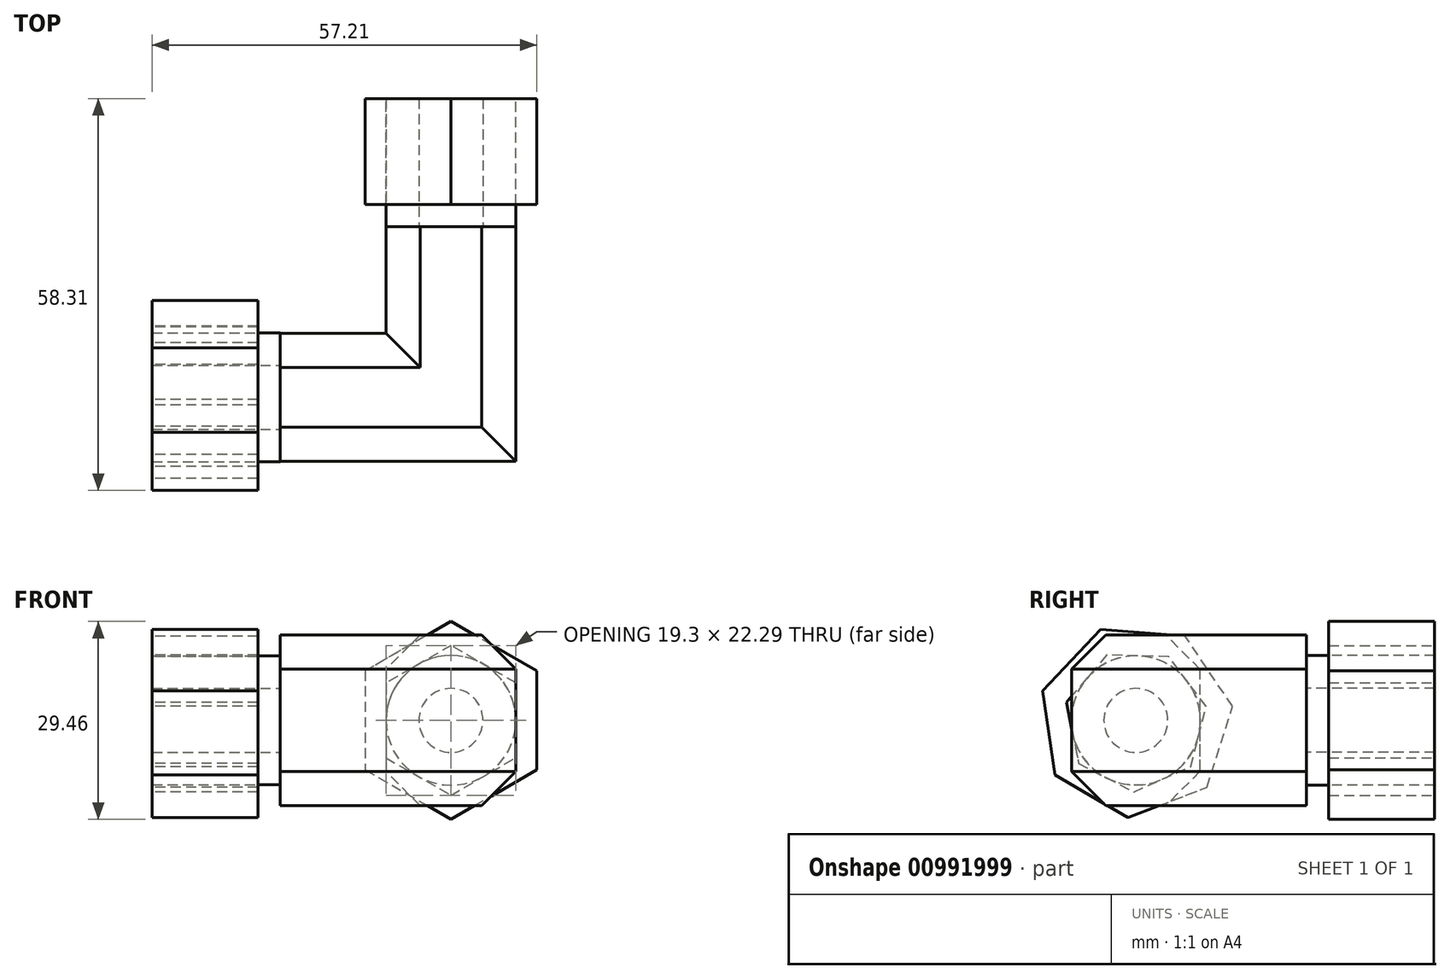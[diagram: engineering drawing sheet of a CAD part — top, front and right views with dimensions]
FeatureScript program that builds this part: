
annotation { "Feature Type Name" : "Feature", "Feature Type Description" : "" }
export const myFeature = defineFeature(function(context is Context, id is Id, definition is map)
    precondition{}
    {
        {
            var Q0;
            Q0=qCreatedBy(makeId("Top.planeOp"),FACE);
            var sketch = newSketch(context, id + "F0", { "sketchPlane" : qUnion([Q0])});
            skLineSegment(sketch, "E0", {"start": v(0, 0) * mm, "end": v(0, 25.4) * mm, "construction": true});
            skLineSegment(sketch, "E1", {"start": v(0, 0) * mm, "end": v(-25.4, 0) * mm, "construction": true});
            skLineSegment(sketch, "E2", {"start": v(-25.4, 9.52) * mm, "end": v(-9.65, 9.53) * mm});
            skLineSegment(sketch, "E3", {"start": v(-9.65, 9.53) * mm, "end": v(-9.65, 25.4) * mm});
            skLineSegment(sketch, "E4", {"start": v(-9.65, 25.4) * mm, "end": v(0, 25.4) * mm});
            skLineSegment(sketch, "E5", {"start": v(-25.4, 9.52) * mm, "end": v(-25.4, 0) * mm});
            skLineSegment(sketch, "E6.MirrorCS", {"start": v(9.65, 9.53) * mm, "end": v(9.65, 25.4) * mm});
            skLineSegment(sketch, "E7.MirrorCS", {"start": v(9.65, 25.4) * mm, "end": v(0, 25.4) * mm});
            skLineSegment(sketch, "E8.MirrorCS", {"start": v(-25.4, -9.53) * mm, "end": v(-25.4, 0) * mm});
            skLineSegment(sketch, "E9", {"start": v(-25.4, -9.53) * mm, "end": v(9.65, -9.53) * mm});
            skLineSegment(sketch, "E10", {"start": v(9.65, -9.53) * mm, "end": v(9.65, 9.53) * mm});
            skSolve(sketch);
        }
        {
            var Q0;
            Q0=makeQuery(id+"F0.imprint","IMPRINT",FACE,{"disambiguationData":[TD([[makeQuery(id+"F0.imprint","IMPRINT",EDGE,{"derivedFrom":sQuery(id+"F0.wireOp",EDGE,"E2")}),-1.0]])]});
            extrude(context, id + "F1", {"entities" : qUnion([Q0]), "endBound" : BoundingType.SYMMETRIC, "depth" : 25.4 * mm, "offsetDistance" : 25.4 * mm});
        }
        {
            var Q0;
            Q0=makeQuery(id+"F1.opExtrude","SWEPT_FACE",FACE,{"disambiguationData":[OSD([sQuery(id+"F0.wireOp",EDGE,"E5"),sQuery(id+"F0.wireOp",EDGE,"E8.MirrorCS")])]});
            var sketch = newSketch(context, id + "F2", { "sketchPlane" : qUnion([Q0])});
            skCircle(sketch, "E11", {"center": v(0, 0) * mm, "radius": 9.6 * mm});
            skCircle(sketch, "E12", {"center": v(0, 0) * mm, "radius": 4.76 * mm});
            skSolve(sketch);
        }
        {
            var Q0;
            Q0 = qSketchRegion(id + "F2", true);
            extrude(context, id + "F3", {"entities" : qUnion([Q0]), "operationType" : NewBodyOperationType.ADD, "depth" : 19.05 * mm, "offsetDistance" : 25.4 * mm});
        }
        {
            var Q0;
            Q0=makeQuery(id+"F3.opExtrude","CAP_FACE",FACE,{"disambiguationData":[OSD([sQuery(id+"F2.wireOp",EDGE,"E11"),sQuery(id+"F2.wireOp",EDGE,"E12")])],"isStart":false});
            var sketch = newSketch(context, id + "F4", { "sketchPlane" : qUnion([Q0])});
            skCircle(sketch, "E13.cCircle", {"center": v(0, 0) * mm, "radius": 9.6 * mm, "construction": true});
            skLineSegment(sketch, "E13.0", {"start": v(10.32, 2.66) * mm, "end": v(8.52, -6.41) * mm});
            skLineSegment(sketch, "E13.1", {"start": v(8.52, -6.41) * mm, "end": v(0.3, -10.66) * mm});
            skLineSegment(sketch, "E13.2", {"start": v(0.3, -10.66) * mm, "end": v(-8.15, -6.88) * mm});
            skLineSegment(sketch, "E13.3", {"start": v(-8.15, -6.88) * mm, "end": v(-10.46, 2.08) * mm});
            skLineSegment(sketch, "E13.4", {"start": v(-10.46, 2.08) * mm, "end": v(-4.9, 9.47) * mm});
            skLineSegment(sketch, "E13.5", {"start": v(-4.9, 9.47) * mm, "end": v(4.35, 9.73) * mm});
            skLineSegment(sketch, "E13.6", {"start": v(4.35, 9.73) * mm, "end": v(10.32, 2.66) * mm});
            skPoint(sketch, "E13.0.midPoint", {"position": v(9.42, -1.87) * mm});
            skCircle(sketch, "E14.cCircle", {"center": v(0, 0) * mm, "radius": 13.1 * mm, "construction": true});
            skLineSegment(sketch, "E14.0", {"start": v(13.86, 4.37) * mm, "end": v(12.05, -8.11) * mm});
            skLineSegment(sketch, "E14.1", {"start": v(12.05, -8.11) * mm, "end": v(1.17, -14.48) * mm});
            skLineSegment(sketch, "E14.2", {"start": v(1.17, -14.48) * mm, "end": v(-10.6, -9.95) * mm});
            skLineSegment(sketch, "E14.3", {"start": v(-10.6, -9.95) * mm, "end": v(-14.38, 2.08) * mm});
            skLineSegment(sketch, "E14.4", {"start": v(-14.38, 2.08) * mm, "end": v(-7.34, 12.54) * mm});
            skLineSegment(sketch, "E14.5", {"start": v(-7.34, 12.54) * mm, "end": v(5.23, 13.56) * mm});
            skLineSegment(sketch, "E14.6", {"start": v(5.23, 13.56) * mm, "end": v(13.86, 4.37) * mm});
            skPoint(sketch, "E14.0.midPoint", {"position": v(12.96, -1.87) * mm});
            skSolve(sketch);
        }
        {
            var Q0;
            Q0 = qSketchRegion(id + "F4", true);
            extrude(context, id + "F5", {"entities" : qUnion([Q0]), "operationType" : NewBodyOperationType.ADD, "oppositeDirection" : true, "depth" : 15.75 * mm, "offsetDistance" : 25.4 * mm});
        }
        {
            var Q0;
            Q0=makeQuery(id+"F1.opExtrude","SWEPT_FACE",FACE,{"disambiguationData":[OSD([sQuery(id+"F0.wireOp",EDGE,"E4"),sQuery(id+"F0.wireOp",EDGE,"E7.MirrorCS")])]});
            var sketch = newSketch(context, id + "F6", { "sketchPlane" : qUnion([Q0])});
            skCircle(sketch, "E15", {"center": v(0, 0) * mm, "radius": 9.65 * mm});
            skCircle(sketch, "E16", {"center": v(0, 0) * mm, "radius": 4.76 * mm});
            skSolve(sketch);
        }
        {
            var Q0;
            Q0 = qSketchRegion(id + "F6", true);
            extrude(context, id + "F7", {"entities" : qUnion([Q0]), "operationType" : NewBodyOperationType.ADD, "depth" : 19.05 * mm, "offsetDistance" : 25.4 * mm});
        }
        {
            var Q0;
            Q0=makeQuery(id+"F7.opExtrude","CAP_FACE",FACE,{"disambiguationData":[OSD([sQuery(id+"F6.wireOp",EDGE,"E15"),sQuery(id+"F6.wireOp",EDGE,"E16")])],"isStart":false});
            var sketch = newSketch(context, id + "F8", { "sketchPlane" : qUnion([Q0])});
            skCircle(sketch, "E17.cCircle", {"center": v(0, 0) * mm, "radius": 9.65 * mm, "construction": true});
            skLineSegment(sketch, "E17.0", {"start": v(9.65, 5.57) * mm, "end": v(9.65, -5.57) * mm});
            skLineSegment(sketch, "E17.1", {"start": v(9.65, -5.57) * mm, "end": v(0, -11.15) * mm});
            skLineSegment(sketch, "E17.2", {"start": v(0, -11.15) * mm, "end": v(-9.65, -5.57) * mm});
            skLineSegment(sketch, "E17.3", {"start": v(-9.65, -5.57) * mm, "end": v(-9.65, 5.57) * mm});
            skLineSegment(sketch, "E17.4", {"start": v(-9.65, 5.57) * mm, "end": v(0, 11.15) * mm});
            skLineSegment(sketch, "E17.5", {"start": v(0, 11.15) * mm, "end": v(9.65, 5.57) * mm});
            skPoint(sketch, "E17.0.midPoint", {"position": v(9.65, 0) * mm});
            skCircle(sketch, "E18.cCircle", {"center": v(0, 0) * mm, "radius": 12.76 * mm, "construction": true});
            skLineSegment(sketch, "E18.0", {"start": v(12.76, 7.37) * mm, "end": v(12.76, -7.37) * mm});
            skLineSegment(sketch, "E18.1", {"start": v(12.76, -7.37) * mm, "end": v(0, -14.73) * mm});
            skLineSegment(sketch, "E18.2", {"start": v(0, -14.73) * mm, "end": v(-12.76, -7.37) * mm});
            skLineSegment(sketch, "E18.3", {"start": v(-12.76, -7.37) * mm, "end": v(-12.76, 7.37) * mm});
            skLineSegment(sketch, "E18.4", {"start": v(-12.76, 7.37) * mm, "end": v(0, 14.73) * mm});
            skLineSegment(sketch, "E18.5", {"start": v(0, 14.73) * mm, "end": v(12.76, 7.37) * mm});
            skPoint(sketch, "E18.0.midPoint", {"position": v(12.76, 0) * mm});
            skSolve(sketch);
        }
        {
            var Q0;
            Q0 = qSketchRegion(id + "F8", true);
            extrude(context, id + "F9", {"entities" : qUnion([Q0]), "oppositeDirection" : true, "depth" : 15.75 * mm, "offsetDistance" : 25.4 * mm});
        }
        {
            var Q0;
            Q0=makeQuery(id+"F1.opExtrude","CAP_EDGE",EDGE,{"disambiguationData":[OSD([sQuery(id+"F0.wireOp",EDGE,"E2")])],"isStart":false});
            var Q1;
            Q1=makeQuery(id+"F1.opExtrude","CAP_EDGE",EDGE,{"disambiguationData":[OSD([sQuery(id+"F0.wireOp",EDGE,"E9")])],"isStart":false});
            var Q2;
            Q2=makeQuery(id+"F1.opExtrude","CAP_EDGE",EDGE,{"disambiguationData":[OSD([sQuery(id+"F0.wireOp",EDGE,"E3")])],"isStart":false});
            var Q3;
            Q3=makeQuery(id+"F1.opExtrude","CAP_EDGE",EDGE,{"disambiguationData":[OSD([sQuery(id+"F0.wireOp",EDGE,"E6.MirrorCS"),sQuery(id+"F0.wireOp",EDGE,"E10")])],"isStart":false});
            var Q4;
            Q4=makeQuery(id+"F1.opExtrude","CAP_EDGE",EDGE,{"disambiguationData":[OSD([sQuery(id+"F0.wireOp",EDGE,"E6.MirrorCS"),sQuery(id+"F0.wireOp",EDGE,"E10")])],"isStart":true});
            var Q5;
            Q5=makeQuery(id+"F1.opExtrude","CAP_EDGE",EDGE,{"disambiguationData":[OSD([sQuery(id+"F0.wireOp",EDGE,"E2")])],"isStart":true});
            var Q6;
            Q6=makeQuery(id+"F1.opExtrude","CAP_EDGE",EDGE,{"disambiguationData":[OSD([sQuery(id+"F0.wireOp",EDGE,"E3")])],"isStart":true});
            var Q7;
            Q7=makeQuery(id+"F1.opExtrude","CAP_EDGE",EDGE,{"disambiguationData":[OSD([sQuery(id+"F0.wireOp",EDGE,"E9")])],"isStart":true});
            chamfer(context, id + "F10", {"entities" : qUnion([Q0, Q1, Q2, Q3, Q4, Q5, Q6, Q7]), "width" : 5.08 * mm, "tangentPropagation" : true});
        }
    });
